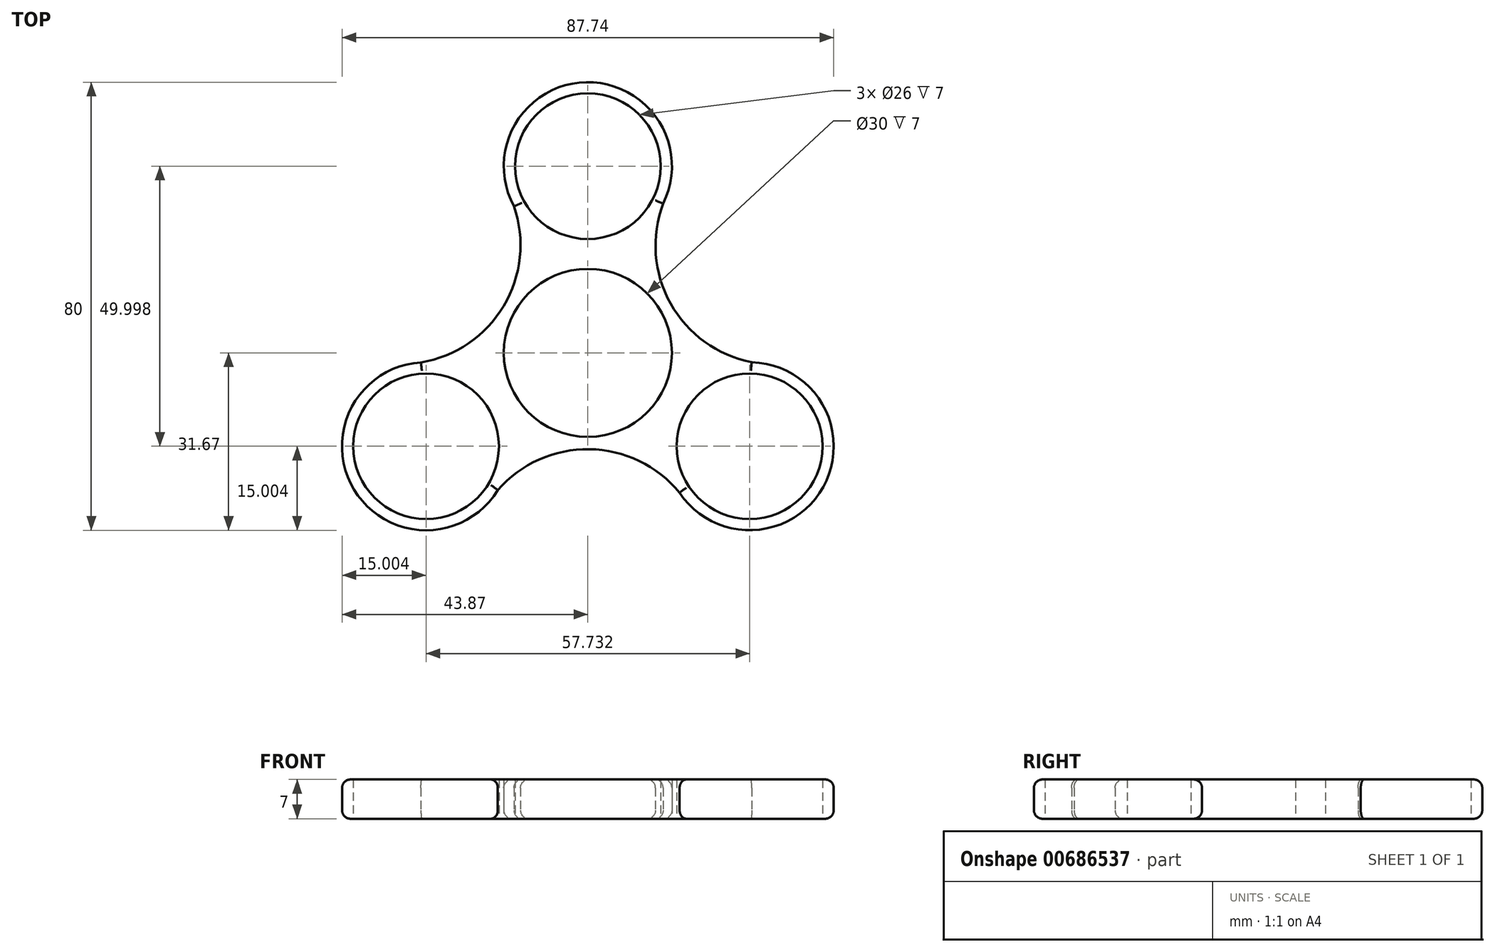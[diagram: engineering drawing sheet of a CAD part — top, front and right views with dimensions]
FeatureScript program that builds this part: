
annotation { "Feature Type Name" : "Feature", "Feature Type Description" : "" }
export const myFeature = defineFeature(function(context is Context, id is Id, definition is map)
    precondition{}
    {
        {
            var Q0;
            Q0=qCreatedBy(makeId("Top.planeOp"),FACE);
            var sketch = newSketch(context, id + "F0", { "sketchPlane" : qUnion([Q0])});
            skCircle(sketch, "E0", {"center": v(0, 0) * mm, "radius": 13 * mm});
            skCircle(sketch, "E1", {"center": v(0, 33.33) * mm, "radius": 13 * mm});
            skPoint(sketch, "E2.center", {"position": v(-0.15, -0.28) * mm});
            skCircle(sketch, "E3", {"center": v(0, 0) * mm, "radius": 15 * mm});
            skArc(sketch, "E4", {"start": v(13.43, 26.65) * mm, "mid": v(-0.27, 48.33) * mm, "end": v(-13.18, 26.16) * mm});
            skArc(sketch, "E5.1.0", {"start": v(-29.8, -1.7) * mm, "mid": v(-41.72, -24.4) * mm, "end": v(-16.07, -24.5) * mm});
            skCircle(sketch, "E5.1.1", {"center": v(-28.87, -16.67) * mm, "radius": 13 * mm});
            skArc(sketch, "E5.2.0", {"start": v(16.36, -24.95) * mm, "mid": v(42, -23.93) * mm, "end": v(29.24, -1.67) * mm});
            skCircle(sketch, "E5.2.1", {"center": v(28.87, -16.67) * mm, "radius": 13 * mm});
            skArc(sketch, "E6", {"start": v(13.43, 26.65) * mm, "mid": v(14.76, 8.82) * mm, "end": v(29.24, -1.67) * mm});
            skArc(sketch, "E7.1.0", {"start": v(-29.8, -1.7) * mm, "mid": v(-15.02, 8.38) * mm, "end": v(-13.18, 26.16) * mm});
            skArc(sketch, "E7.2.0", {"start": v(16.36, -24.95) * mm, "mid": v(0.25, -17.2) * mm, "end": v(-16.07, -24.5) * mm});
            skLineSegment(sketch, "E8.trimOffspring", {"start": v(11.46, 6.14) * mm, "end": v(15.12, 8.21) * mm, "construction": true});
            skLineSegment(sketch, "E9.trimOffspring", {"start": v(-12.9, -7.64) * mm, "end": v(-11.17, -6.65) * mm, "construction": true});
            skSolve(sketch);
        }
        {
            var Q0;
            Q0=makeQuery(id+"F0.imprint","IMPRINT",FACE,{"disambiguationData":[TD([[makeQuery(id+"F0.imprint","IMPRINT",EDGE,{"derivedFrom":sQuery(id+"F0.wireOp",EDGE,"E1")}),-1.0]])]});
            extrude(context, id + "F1", {"entities" : qUnion([Q0]), "depth" : 7 * mm, "offsetDistance" : 25 * mm});
        }
        {
            var Q0;
            Q0=makeQuery(id+"F1.opExtrude","CAP_EDGE",EDGE,{"disambiguationData":[OSD([sQuery(id+"F0.wireOp",EDGE,"E2.1.0")])],"isStart":false});
            var Q1;
            Q1=makeQuery(id+"F1.opExtrude","CAP_EDGE",EDGE,{"disambiguationData":[OSD([sQuery(id+"F0.wireOp",EDGE,"85137b85-7345-46bd-88c1-d651f43c9508.2.0")])],"isStart":false});
            var Q2;
            Q2=makeQuery(id+"F1.opExtrude","CAP_EDGE",EDGE,{"disambiguationData":[OSD([sQuery(id+"F0.wireOp",EDGE,"85137b85-7345-46bd-88c1-d651f43c9508.1.0")])],"isStart":false});
            var Q3;
            Q3=makeQuery(id+"F1.opExtrude","CAP_EDGE",EDGE,{"disambiguationData":[OSD([sQuery(id+"F0.wireOp",EDGE,"74z2S9nH-pUj3-VOHU-keD0-TOjbiJOuWvYw")])],"isStart":false});
            var Q4;
            Q4=makeQuery(id+"F1.opExtrude","CAP_EDGE",EDGE,{"disambiguationData":[OSD([sQuery(id+"F0.wireOp",EDGE,"Ok7rsxyM-kMHL-MHV5-iMG4-qb0Bb9I3xXih")])],"isStart":false});
            var Q5;
            Q5=makeQuery(id+"F1.opExtrude","CAP_EDGE",EDGE,{"disambiguationData":[OSD([sQuery(id+"F0.wireOp",EDGE,"E2.2.0")])],"isStart":false});
            var Q6;
            Q6=makeQuery(id+"F1.opExtrude","CAP_EDGE",EDGE,{"disambiguationData":[OSD([sQuery(id+"F0.wireOp",EDGE,"74z2S9nH-pUj3-VOHU-keD0-TOjbiJOuWvYw")])],"isStart":true});
            var Q7;
            Q7=makeQuery(id+"F1.opExtrude","CAP_EDGE",EDGE,{"disambiguationData":[OSD([sQuery(id+"F0.wireOp",EDGE,"Ok7rsxyM-kMHL-MHV5-iMG4-qb0Bb9I3xXih")])],"isStart":true});
            var Q8;
            Q8=makeQuery(id+"F1.opExtrude","CAP_EDGE",EDGE,{"disambiguationData":[OSD([sQuery(id+"F0.wireOp",EDGE,"85137b85-7345-46bd-88c1-d651f43c9508.1.0")])],"isStart":true});
            var Q9;
            Q9=makeQuery(id+"F1.opExtrude","CAP_EDGE",EDGE,{"disambiguationData":[OSD([sQuery(id+"F0.wireOp",EDGE,"E2.1.0")])],"isStart":true});
            var Q10;
            Q10=makeQuery(id+"F1.opExtrude","CAP_EDGE",EDGE,{"disambiguationData":[OSD([sQuery(id+"F0.wireOp",EDGE,"85137b85-7345-46bd-88c1-d651f43c9508.2.0")])],"isStart":true});
            var Q11;
            Q11=makeQuery(id+"F1.opExtrude","CAP_EDGE",EDGE,{"disambiguationData":[OSD([sQuery(id+"F0.wireOp",EDGE,"E2.2.0")])],"isStart":true});
            var Q12;
            Q12=makeQuery(id+"F1.opExtrude","CAP_EDGE",EDGE,{"disambiguationData":[OSD([sQuery(id+"F0.wireOp",EDGE,"E7.2.0")])],"isStart":false});
            var Q13;
            Q13=makeQuery(id+"F1.opExtrude","CAP_EDGE",EDGE,{"disambiguationData":[OSD([sQuery(id+"F0.wireOp",EDGE,"E5.1.0")])],"isStart":false});
            var Q14;
            Q14=makeQuery(id+"F1.opExtrude","CAP_EDGE",EDGE,{"disambiguationData":[OSD([sQuery(id+"F0.wireOp",EDGE,"E7.1.0")])],"isStart":false});
            var Q15;
            Q15=makeQuery(id+"F1.opExtrude","CAP_EDGE",EDGE,{"disambiguationData":[OSD([sQuery(id+"F0.wireOp",EDGE,"E6")])],"isStart":false});
            var Q16;
            Q16=makeQuery(id+"F1.opExtrude","CAP_EDGE",EDGE,{"disambiguationData":[OSD([sQuery(id+"F0.wireOp",EDGE,"E4")])],"isStart":false});
            var Q17;
            Q17=makeQuery(id+"F1.opExtrude","CAP_EDGE",EDGE,{"disambiguationData":[OSD([sQuery(id+"F0.wireOp",EDGE,"E5.2.0")])],"isStart":false});
            var Q18;
            Q18=makeQuery(id+"F1.opExtrude","CAP_EDGE",EDGE,{"disambiguationData":[OSD([sQuery(id+"F0.wireOp",EDGE,"E7.2.0")])],"isStart":true});
            var Q19;
            Q19=makeQuery(id+"F1.opExtrude","CAP_EDGE",EDGE,{"disambiguationData":[OSD([sQuery(id+"F0.wireOp",EDGE,"E5.1.0")])],"isStart":true});
            var Q20;
            Q20=makeQuery(id+"F1.opExtrude","CAP_EDGE",EDGE,{"disambiguationData":[OSD([sQuery(id+"F0.wireOp",EDGE,"E7.1.0")])],"isStart":true});
            var Q21;
            Q21=makeQuery(id+"F1.opExtrude","CAP_EDGE",EDGE,{"disambiguationData":[OSD([sQuery(id+"F0.wireOp",EDGE,"E4")])],"isStart":true});
            var Q22;
            Q22=makeQuery(id+"F1.opExtrude","CAP_EDGE",EDGE,{"disambiguationData":[OSD([sQuery(id+"F0.wireOp",EDGE,"E6")])],"isStart":true});
            var Q23;
            Q23=makeQuery(id+"F1.opExtrude","CAP_EDGE",EDGE,{"disambiguationData":[OSD([sQuery(id+"F0.wireOp",EDGE,"E5.2.0")])],"isStart":true});
            fillet(context, id + "F2", {"entities" : qUnion([Q0, Q1, Q2, Q3, Q4, Q5, Q6, Q7, Q8, Q9, Q10, Q11, Q12, Q13, Q14, Q15, Q16, Q17, Q18, Q19, Q20, Q21, Q22, Q23]), "radius" : 1.5 * mm, "tangentPropagation" : true, "allowEdgeOverflow" : false});
        }
    });
